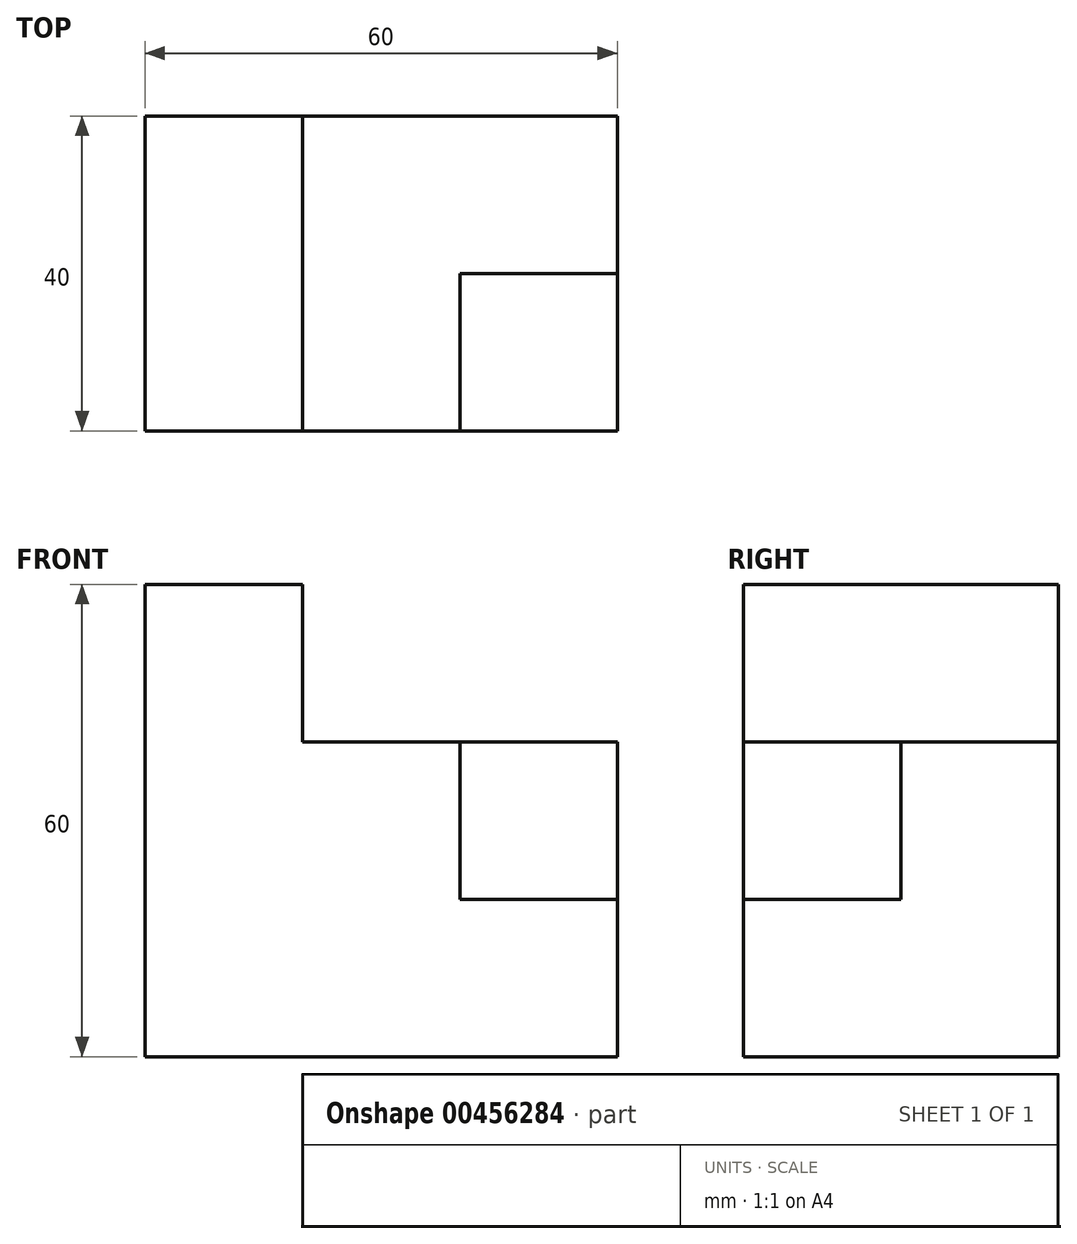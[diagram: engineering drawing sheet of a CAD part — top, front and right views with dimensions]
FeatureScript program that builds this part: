
annotation { "Feature Type Name" : "Feature", "Feature Type Description" : "" }
export const myFeature = defineFeature(function(context is Context, id is Id, definition is map)
    precondition{}
    {
        {
            var Q0;
            Q0=qCreatedBy(makeId("Front.planeOp"),FACE);
            var sketch = newSketch(context, id + "F0", { "sketchPlane" : qUnion([Q0])});
            skLineSegment(sketch, "E0", {"start": v(0, 0) * mm, "end": v(60, 0) * mm});
            skLineSegment(sketch, "E1", {"start": v(60, 0) * mm, "end": v(60, 20) * mm});
            skLineSegment(sketch, "E2", {"start": v(60, 20) * mm, "end": v(40, 20) * mm});
            skLineSegment(sketch, "E3", {"start": v(40, 20) * mm, "end": v(40, 40) * mm});
            skLineSegment(sketch, "E4", {"start": v(40, 40) * mm, "end": v(20, 40) * mm});
            skLineSegment(sketch, "E5", {"start": v(20, 40) * mm, "end": v(20, 60) * mm});
            skLineSegment(sketch, "E6", {"start": v(20, 60) * mm, "end": v(0, 60) * mm});
            skLineSegment(sketch, "E7", {"start": v(0, 60) * mm, "end": v(0, 0) * mm});
            skLineSegment(sketch, "E8", {"start": v(40, 40) * mm, "end": v(60, 40) * mm});
            skLineSegment(sketch, "E9", {"start": v(60, 40) * mm, "end": v(60, 20) * mm});
            skSolve(sketch);
        }
        {
            var Q0;
            Q0=makeQuery(id+"F0.imprint","IMPRINT",FACE,{"disambiguationData":[TD([[makeQuery(id+"F0.imprint","IMPRINT",EDGE,{"derivedFrom":sQuery(id+"F0.wireOp",EDGE,"E0")}),1.0]])]});
            extrude(context, id + "F1", {"entities" : qUnion([Q0]), "endBound" : BoundingType.SYMMETRIC, "depth" : 40 * mm});
        }
        {
            var Q0;
            Q0 = qSketchRegion(id + "F0", true);
            extrude(context, id + "F2", {"entities" : qUnion([Q0]), "operationType" : NewBodyOperationType.ADD, "oppositeDirection" : true, "depth" : 20 * mm});
        }
    });
